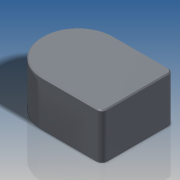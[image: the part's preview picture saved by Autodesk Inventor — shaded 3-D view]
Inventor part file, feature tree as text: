
AUTODESK INVENTOR PART (.ipt)
format: ipt  version: 2016 SP2 (Build 200236200, 236)  size: 110,080 bytes
history: native  units: in
note: dims shown in document units (in); Inventor stores cm internally (conversion verified against a paired STEP export)
features: extrude x1, fillet x1, chamfer x1, sketch x1
ambient origin geometry x8: Origin, YZ Plane, XZ Plane, XY Plane, X Axis, Y Axis, Z Axis, Center Point
bodies: Solid1 (feature_tree)
feature tree (4):
  extrude  "Extrusion1"  Depth=0.0236in
  fillet  "Fillet1"  Radius=0.2047in
  chamfer  "Chamfer1"  Distance=0.0236in
  sketch  "Sketch2"  dims[d0=0.3213in d1=0.2677in d2=0.2047in d3=0.0in d4=0.0236in d5=0.0047in d6=0.0787in d7=45.0deg]
